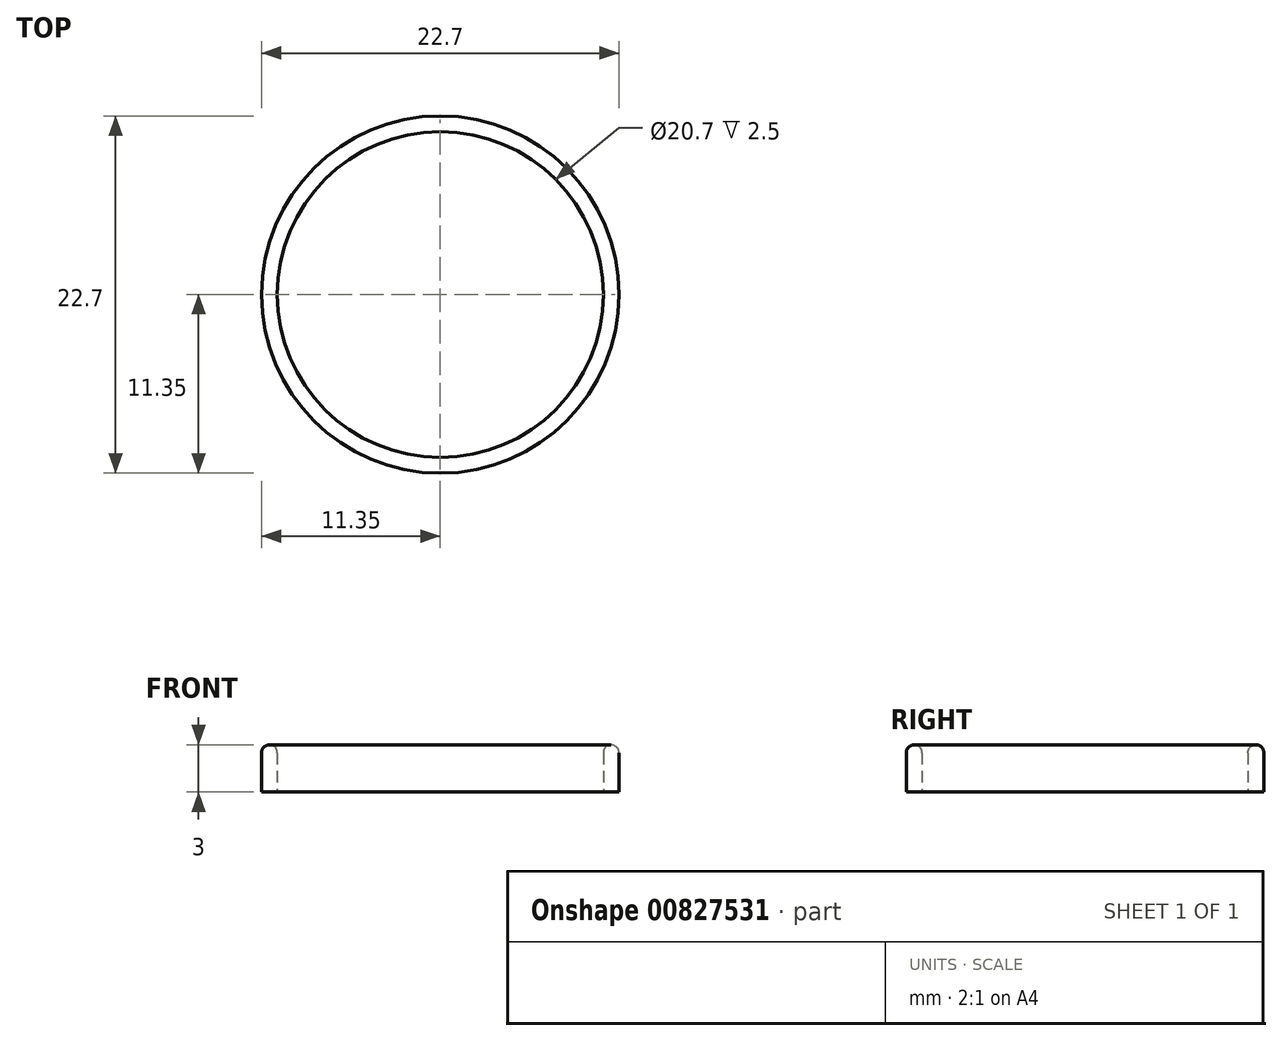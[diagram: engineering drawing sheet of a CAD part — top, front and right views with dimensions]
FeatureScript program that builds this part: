
annotation { "Feature Type Name" : "Feature", "Feature Type Description" : "" }
export const myFeature = defineFeature(function(context is Context, id is Id, definition is map)
    precondition{}
    {
        {
            var Q0;
            Q0=qCreatedBy(makeId("Top.planeOp"),FACE);
            var sketch = newSketch(context, id + "F0", { "sketchPlane" : qUnion([Q0])});
            skCircle(sketch, "E0", {"center": v(0, 0) * mm, "radius": 10.35 * mm});
            skCircle(sketch, "E1", {"center": v(0, 0) * mm, "radius": 11.35 * mm});
            skSolve(sketch);
        }
        {
            var Q0;
            Q0=makeQuery(id+"F0.imprint","IMPRINT",FACE,{"disambiguationData":[TD([[makeQuery(id+"F0.imprint","IMPRINT",EDGE,{"derivedFrom":sQuery(id+"F0.wireOp",EDGE,"E0")}),-1.0]])]});
            extrude(context, id + "F1", {"entities" : qUnion([Q0]), "depth" : 3 * mm, "offsetDistance" : 25 * mm});
        }
        {
            var Q0;
            Q0=makeQuery(id+"F1.opExtrude","CAP_FACE",FACE,{"disambiguationData":[OSD([sQuery(id+"F0.wireOp",EDGE,"E0"),sQuery(id+"F0.wireOp",EDGE,"E1")])],"isStart":false});
            fillet(context, id + "F2", {"entities" : qUnion([Q0]), "radius" : .5 * mm, "tangentPropagation" : true, "allowEdgeOverflow" : false});
        }
    });
